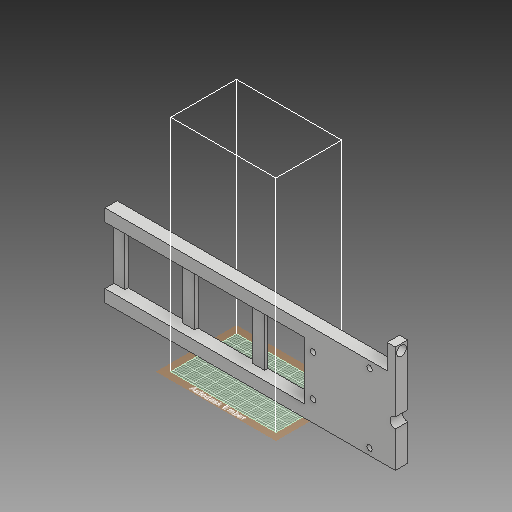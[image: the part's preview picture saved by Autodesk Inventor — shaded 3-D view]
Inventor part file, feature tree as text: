
AUTODESK INVENTOR PART (.ipt)
format: ipt  version: 2018 (Build 220112000, 112)  size: 1,129,984 bytes
history: native  units: mm
features: sketch x81, extrude x64, fillet x22, hole x8
ambient origin geometry x8: Origin, YZ Plane, XZ Plane, XY Plane, X Axis, Y Axis, Z Axis, Center Point
bodies: Solid1 (feature_tree)
feature tree (175):
  extrude  "Extrusion1"  Depth=50.0mm
  hole  "Hole1"  [1 undecoded]
  hole  "Hole2"  [1 undecoded]
  extrude  "Extrusion2"  Depth=25.0mm
  extrude  "Extrusion3"  Depth=25.0mm
  extrude  "Extrusion4"  Depth=5.0mm
  sketch  "Sketch7"  dims[d25=10.0mm d26=5.0mm]
  extrude  "Extrusion5"  Depth=5.0mm
  extrude  "Extrusion6"  Depth=35.0mm
  extrude  "Extrusion7"  Depth=35.0mm
  extrude  "Extrusion8"  Depth=35.0mm
  extrude  "Extrusion9"  Depth=2.0mm TaperAngle=0.0deg
  extrude  "Extrusion10"  Depth=7.5mm TaperAngle=0.0deg
  extrude  "Extrusion11"  Depth=10.0mm
  extrude  "Extrusion12"  Depth=7.5mm
  fillet  "Fillet1"  Radius=7.5mm
  fillet  "Fillet2"  Radius=25.0mm
  fillet  "Fillet3"  Radius=3.0mm
  fillet  "Fillet4"  Radius=3.2mm
  fillet  "Fillet5"  Radius=2.1mm
  fillet  "Fillet6"  Radius=5.5mm
  extrude  "Extrusion13"  Depth=92.5mm TaperAngle=0.0deg
  sketch  "Sketch17"  dims[d58=4.25mm d59=241.0mm d60=0.0mm]
  hole  "Hole3"  [1 undecoded]
  hole  "Hole4"  [1 undecoded]
  extrude  "Extrusion14"  Depth=5.0mm
  extrude  "Extrusion15"  Depth=2.5mm TaperAngle=0.0deg
  extrude  "Extrusion16"  Depth=6.35mm
  extrude  "Extrusion17"  Depth=2.5mm
  extrude  "Extrusion18"  Depth=14.55mm TaperAngle=0.0deg
  extrude  "Extrusion19"  Depth=0.1mm
  extrude  "Extrusion20"  Depth=3.25mm
  extrude  "Extrusion21"  Depth=3.25mm
  hole  "Hole5"  [1 undecoded]
  extrude  "Extrusion22"  Depth=2.0mm
  extrude  "Extrusion23"  Depth=15.0mm
  extrude  "Extrusion24"  Depth=10.0mm TaperAngle=0.0deg
  hole  "Hole6"  [1 undecoded]
  extrude  "Extrusion25"  Depth=100.0mm TaperAngle=0.0deg
  extrude  "Extrusion26"  Depth=2.0mm TaperAngle=0.0deg
  extrude  "Extrusion27"  Depth=3.3mm
  extrude  "Extrusion28"  Depth=3.3mm
  hole  "Hole7"  [1 undecoded]
  extrude  "Extrusion29"  Depth=8.0mm
  extrude  "Extrusion30"  Depth=17.0mm
  hole  "Hole8"  [1 undecoded]
  extrude  "Extrusion31"  Depth=3.5mm
  extrude  "Extrusion32"  Depth=10.0mm
  fillet  "Fillet7"  Radius=3.3mm
  fillet  "Fillet8"  Radius=10.0mm
  extrude  "Extrusion33"  Depth=5.0mm
  extrude  "Extrusion34"  Depth=5.0mm
  sketch  "Sketch45"  dims[d149=10.0mm d150=17.5mm d151=0.0mm]
  sketch  "Sketch46"  dims[d152=5.0mm]
  extrude  "Extrusion35"  Depth=10.0mm TaperAngle=0.0deg
  extrude  "Extrusion36"  Depth=8.0mm TaperAngle=0.0deg
  extrude  "Extrusion37"  Depth=3.75mm
  extrude  "Extrusion38"  Depth=3.75mm
  extrude  "Extrusion39"  Depth=10.0mm TaperAngle=0.0deg
  extrude  "Extrusion40"  Depth=2.0mm TaperAngle=0.0deg
  fillet  "Fillet9"  Radius=5.0mm
  fillet  "Fillet10"  Radius=15.0mm
  fillet  "Fillet11"  Radius=7.5mm
  fillet  "Fillet12"  Radius=17.5mm
  extrude  "Extrusion41"  Depth=47.5mm
  extrude  "Extrusion42"  Depth=5.0mm
  sketch  "Sketch55"  dims[d200=20.0mm d203=5.0mm]
  extrude  "Extrusion43"  Depth=5.0mm
  extrude  "Extrusion44"  Depth=7.5mm TaperAngle=0.0deg
  extrude  "Extrusion45"  Depth=4.0mm
  extrude  "Extrusion46"  Depth=12.0mm
  extrude  "Extrusion47"  Depth=7.5mm
  extrude  "Extrusion48"  Depth=20.0mm TaperAngle=0.0deg
  extrude  "Extrusion49"  Depth=20.0mm
  extrude  "Extrusion50"  Depth=4.0mm
  extrude  "Extrusion51"  Depth=10.0mm TaperAngle=0.0deg
  extrude  "Extrusion52"  Depth=5.5mm TaperAngle=0.0deg
  fillet  "Fillet13"  Radius=10.0mm
  fillet  "Fillet14"  Radius=74.724mm
  fillet  "Fillet15"  Radius=74.724mm
  fillet  "Fillet16"  Radius=85.515mm
  extrude  "Extrusion53"  Depth=5.0mm
  extrude  "Extrusion54"  Depth=5.0mm
  fillet  "Fillet17"  Radius=85.515mm
  extrude  "Extrusion55"  Depth=2.0mm TaperAngle=0.0deg
  fillet  "Fillet18"  Radius=2.0mm
  extrude  "Extrusion56"  Depth=2.0mm
  sketch  "Sketch70"  dims[d247=2.0mm d248=10.0mm d249=2.0mm d250=0.0mm d251=1.0mm d252=0.0mm]
  extrude  "Extrusion57"  Depth=10.0mm
  fillet  "Fillet19"  Radius=2.0mm
  fillet  "Fillet20"  Radius=1.0mm
  extrude  "Extrusion58"  Depth=1.0mm TaperAngle=0.0deg
  extrude  "Extrusion59"  Depth=0.349066mm
  fillet  "Fillet21"  Radius=0.349066mm
  sketch  "Sketch74"  dims[d262=4.0mm d263=10.0mm d264=0.0mm]
  extrude  "Extrusion60"  Depth=4.0mm
  sketch  "Sketch76"  dims[d270=3.0mm d271=24.5mm]
  extrude  "Extrusion61"  Depth=10.0mm TaperAngle=0.0deg
  extrude  "Extrusion62"  Depth=6.5mm
  fillet  "Fillet22"  Radius=5.5mm
  sketch  "Sketch79"  dims[d277=7.5mm d278=0.0mm]
  extrude  "Extrusion63"  Depth=24.5mm
  extrude  "Extrusion64"  Depth=5500.0mm TaperAngle=0.0deg
  sketch  "Sketch1"  dims[d0=50.0mm d1=50.0mm]
  sketch  "Sketch2"  dims[d2=240.0mm d3=7.5mm]
  sketch  "Sketch3"  dims[d4=7.5mm d5=7.5mm d6=0.0mm]
  sketch  "Sketch4"  dims[d7=6.35mm d8=6.0mm d9=4.0mm d10=2.0mm d11=90.0deg d12=8.0mm d13=20.594885mm d14=25.0mm]
  sketch  "Sketch5"  dims[d15=3.3mm d16=6.0mm d17=4.0mm d18=2.0mm d19=90.0deg d20=8.0mm d21=20.594885mm d22=25.0mm]
  sketch  "Sketch6"  dims[d23=180.0deg d24=5.0mm]
  sketch  "Sketch8"  dims[d27=17.5mm d28=0.0mm d30=35.0mm]
  sketch  "Sketch9"  dims[d31=35.0mm d32=35.0mm]
  sketch  "Sketch10"  dims[d33=35.0mm d34=35.0mm]
  sketch  "Sketch11"  dims[d35=35.0mm d36=2.0mm d37=0.0mm]
  sketch  "Sketch12"  dims[d38=10.0mm d39=7.5mm d40=0.0mm]
  sketch  "Sketch13"  dims[d41=100.0mm d42=10.0mm]
  sketch  "Sketch14"  dims[d43=7.5mm d44=0.0mm d45=7.5mm d46=7.5mm d47=25.0mm d48=0.0mm d49=3.0mm d50=3.2mm d51=2.1mm d52=5.5mm]
  sketch  "Sketch15"  dims[d53=3.3mm d54=92.5mm d55=0.0mm]
  sketch  "Sketch16"  dims[d56=5.5mm d57=3.3mm]
  sketch  "Sketch18"  dims[d61=4.44mm d62=5.0mm]
  sketch  "Sketch19"  dims[d63=2.5mm d64=91.25mm d65=0.0mm]
  sketch  "Sketch20"  dims[d66=30.0mm d67=6.35mm]
  sketch  "Sketch21"  dims[d68=3.8mm d69=0.0mm d70=2.5mm]
  sketch  "Sketch22"  dims[d71=14.55mm d72=0.0mm d73=14.55mm d74=0.0mm]
  sketch  "Sketch23"  dims[d75=0.1mm d76=0.1mm]
  sketch  "Sketch24"  dims[d77=3.25mm d78=3.25mm]
  sketch  "Sketch25"  dims[d79=3.25mm d80=3.25mm]
  sketch  "Sketch26"  dims[d81=35.0mm d82=10.0mm]
  sketch  "Sketch27"  dims[d83=2.0mm d84=0.0mm d85=3.6mm]
  sketch  "Sketch28"  dims[d86=3.6mm]
  sketch  "Sketch29"  dims[d87=3.3mm d88=6.0mm d89=4.0mm d90=2.0mm d91=90.0deg d92=15.0mm d93=20.594885mm]
  sketch  "Sketch30"  dims[d94=3.3mm d95=6.0mm d96=4.0mm d97=2.0mm d98=90.0deg d99=15.0mm d100=20.594885mm d101=6.0mm]
  sketch  "Sketch31"  dims[d102=20.0mm d103=0.0mm d104=10.0mm d105=0.0mm]
  sketch  "Sketch32"  dims[d106=2.0mm d107=0.0mm d108=4.0mm]
  sketch  "Sketch33"  dims[d109=100.0mm d110=0.0mm d111=100.0mm d112=0.0mm]
  sketch  "Sketch34"  dims[d113=5.0mm d114=2.0mm d115=0.0mm]
  sketch  "Sketch35"  dims[d116=3.3mm d117=3.3mm]
  sketch  "Sketch36"  dims[d118=3.3mm d119=3.3mm]
  sketch  "Sketch37"  dims[d120=2.0mm d121=0.0mm d122=5.5mm d123=0.0mm]
  sketch  "Sketch38"  dims[d124=3.3mm d125=6.0mm d126=4.0mm d127=2.0mm d128=90.0deg d129=8.0mm d130=20.594885mm d131=42.0mm]
  sketch  "Sketch39"  dims[d132=17.0mm d133=21.0mm]
  sketch  "Sketch40"  dims[d135=8.5mm d136=15.825mm]
  sketch  "Sketch41"  dims[d137=3.5mm d138=21.0mm]
  sketch  "Sketch42"  dims[d139=3.3mm d140=3.3mm d141=3.3mm d142=10.0mm d143=0.0mm]
  sketch  "Sketch43"  dims[d144=7.5mm d145=0.0mm d146=5.0mm]
  sketch  "Sketch44"  dims[d147=10.0mm d148=5.0mm]
  sketch  "Sketch47"  dims[d153=7.0mm d154=6.0mm d155=4.0mm d156=2.0mm d157=90.0deg d158=8.0mm d159=20.594885mm d160=17.5mm d161=0.0mm]
  sketch  "Sketch48"  dims[d162=170.5mm d163=0.0mm d164=3.75mm]
  sketch  "Sketch49"  dims[d165=3.75mm d166=3.75mm]
  sketch  "Sketch50"  dims[d167=3.75mm d168=10.0mm d169=0.0mm]
  sketch  "Sketch51"  dims[d170=100.0mm d171=0.0mm]
  sketch  "Sketch52"  dims[d172=5.0mm d173=6.0mm d174=4.0mm d175=2.0mm d176=90.0deg d177=15.0mm d178=0.0mm d179=2.0mm d180=0.0mm d181=5.0mm d182=15.0mm d183=0.0mm d184=7.5mm]
  sketch  "Sketch53"  dims[d185=6.0mm d186=6.0mm d187=4.0mm d188=2.0mm d189=90.0deg d190=15.0mm d191=0.0mm d192=17.5mm d193=0.0mm]
  sketch  "Sketch54"  dims[d194=23.75mm d195=47.5mm]
  sketch  "Sketch56"  dims[d204=5.0mm d205=29.0mm]
  sketch  "Sketch57"  dims[d206=29.0mm d207=7.5mm d208=0.0mm]
  sketch  "Sketch58"  dims[d209=4.0mm d210=4.0mm]
  sketch  "Sketch59"  dims[d211=2.0mm d212=0.0mm d213=12.0mm]
  sketch  "Sketch60"  dims[d214=2.0mm d215=0.0mm d216=7.5mm]
  sketch  "Sketch61"  dims[d217=7.5mm d218=20.0mm d219=0.0mm]
  sketch  "Sketch62"  dims[d220=20.0mm d221=3.3mm]
  sketch  "Sketch63"  dims[d222=20.0mm d223=0.0mm d224=4.0mm]
  sketch  "Sketch64"  dims[d225=4.0mm d226=10.0mm d227=0.0mm]
  sketch  "Sketch65"  dims[d228=3.0mm d229=5.5mm d230=0.0mm d231=10.0mm d232=0.0mm d233=74.724mm d234=74.724mm d235=85.515mm]
  sketch  "Sketch66"  dims[d236=5.0mm d237=5.0mm]
  sketch  "Sketch67"  dims[d238=85.515mm d239=5.0mm d240=85.515mm]
  sketch  "Sketch68"  dims[d241=5.0mm d242=2.0mm d243=0.0mm d244=2.0mm]
  sketch  "Sketch69"  dims[d245=2.0mm d246=2.0mm]
  sketch  "Sketch71"  dims[d253=20.0mm d254=1.0mm d255=0.0mm]
  sketch  "Sketch72"  dims[d256=0.5mm d257=0.0mm d258=0.349066mm d259=0.349066mm]
  sketch  "Sketch73"  dims[d260=4.0mm d261=4.0mm]
  sketch  "Sketch75"  dims[d265=5.5mm d266=0.0mm d267=6.5mm d268=5.5mm d269=0.0mm]
  sketch  "Sketch77"  dims[d272=5500.0mm d273=0.0mm d274=5500.0mm d275=0.0mm]
  sketch  "Sketch78"  dims[d276=24.5mm]
  sketch  "Sketch80"  dims[d279=7.5mm d280=0.0mm]
  sketch  "Sketch81"  dims[d281=7.5mm d282=0.0mm d283=2.0mm d284=2.0mm d285=4.0mm d286=1.5mm d287=4.25mm d288=4.25mm d289=7.5mm d290=0.0mm d291=20.025mm d292=10.0mm d293=2.5mm d294=17.0mm d295=0.0mm d296=1.5mm d298=3.0mm d300=3.0mm d301=5.0mm d302=0.0mm d303=1.0mm d304=10.0mm d305=0.0mm d306=8.45mm d307=8.45mm d308=5.5mm d309=9.5mm d310=17.0mm d311=0.0mm d312=2.0mm d313=2.0mm d314=5.5mm d315=0.0mm d316=9.5mm d317=0.0mm d318=2.0mm d321=4.5mm d322=17.0mm d323=0.0mm d324=11.5mm d325=2.88mm d326=2.88mm d327=3.0mm d328=3.0mm d329=2.5mm d330=0.0mm d331=3.0mm d332=2.5mm d333=0.0mm d334=1.0mm d335=11.0mm d336=4.75mm d337=2.0mm d338=0.0mm d339=6.0mm d340=5.5mm d341=0.0mm]
note: 8 required parameter values undecoded (feature->parameter linkage not recoverable at this tier; creation-order binding heuristic only, values carry confidence <= 0.55)
